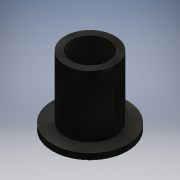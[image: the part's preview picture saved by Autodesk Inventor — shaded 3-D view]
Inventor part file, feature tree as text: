
AUTODESK INVENTOR PART (.ipt)
format: ipt  version: 2016 (Build 200138000, 138)  size: 107,520 bytes
history: native  units: mm
features: extrude x2, other x1, sketch x1
ambient origin geometry x8: Origin, YZ Plane, XZ Plane, XY Plane, X Axis, Y Axis, Z Axis, Center Point
bodies: Body1 (feature_tree)
feature tree (4):
  other  "ソリッド1"
  sketch  "スケッチ1"
  extrude  "押し出し1"  Depth=6.0mm
  extrude  "押し出し2"  Depth=8.0mm
